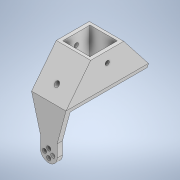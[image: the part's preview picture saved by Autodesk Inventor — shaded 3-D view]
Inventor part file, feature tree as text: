
AUTODESK INVENTOR PART (.ipt)
format: ipt  version: 2022 (Build 260153000, 153)  size: 189,952 bytes
history: native  units: mm
features: extrude x8, sketch x8, plane x1
ambient origin geometry x8: Origin, YZ Plane, XZ Plane, XY Plane, X Axis, Y Axis, Z Axis, Center Point
bodies: Solid1 (feature_tree)
feature tree (17):
  extrude  "Extrusion1"  Depth=4.0mm TaperAngle=360.0deg
  extrude  "Extrusion2"  Depth=5.0mm
  extrude  "Extrusion4"  Depth=73.5mm TaperAngle=0.0deg
  extrude  "Extrusion5"  Depth=12.7mm
  extrude  "Extrusion6"  Depth=3.0mm
  extrude  "Extrusion7"  Depth=3.0mm TaperAngle=0.0deg
  plane  "Work Plane1"
  extrude  "Extrusion8"  Depth=26.0mm
  extrude  "Extrusion9"  Depth=25.4mm TaperAngle=0.0deg
  sketch  "Sketch1"  dims[d2=4.0mm d3=40.0mm d5=360.0deg]
  sketch  "Sketch2"  dims[d16=5.0mm d17=0.0mm d18=13.25mm]
  sketch  "Sketch4"  dims[d19=2.0mm d20=0.0mm d26=73.5mm d27=0.0mm]
  sketch  "Sketch5"  dims[d28=30.0mm d29=0.0mm d30=12.7mm]
  sketch  "Sketch6"  dims[d31=12.7mm d32=3.0mm]
  sketch  "Sketch7"  dims[d33=3.0mm d34=30.0mm d35=0.0mm]
  sketch  "Sketch8"  dims[d37=13.0mm d38=26.0mm]
  sketch  "Sketch9"  dims[d39=26.0mm d40=25.4mm d41=0.0mm d43=4.0mm d44=0.0mm d45=0.0mm d47=4.0mm d48=10.0mm d49=0.0mm]
